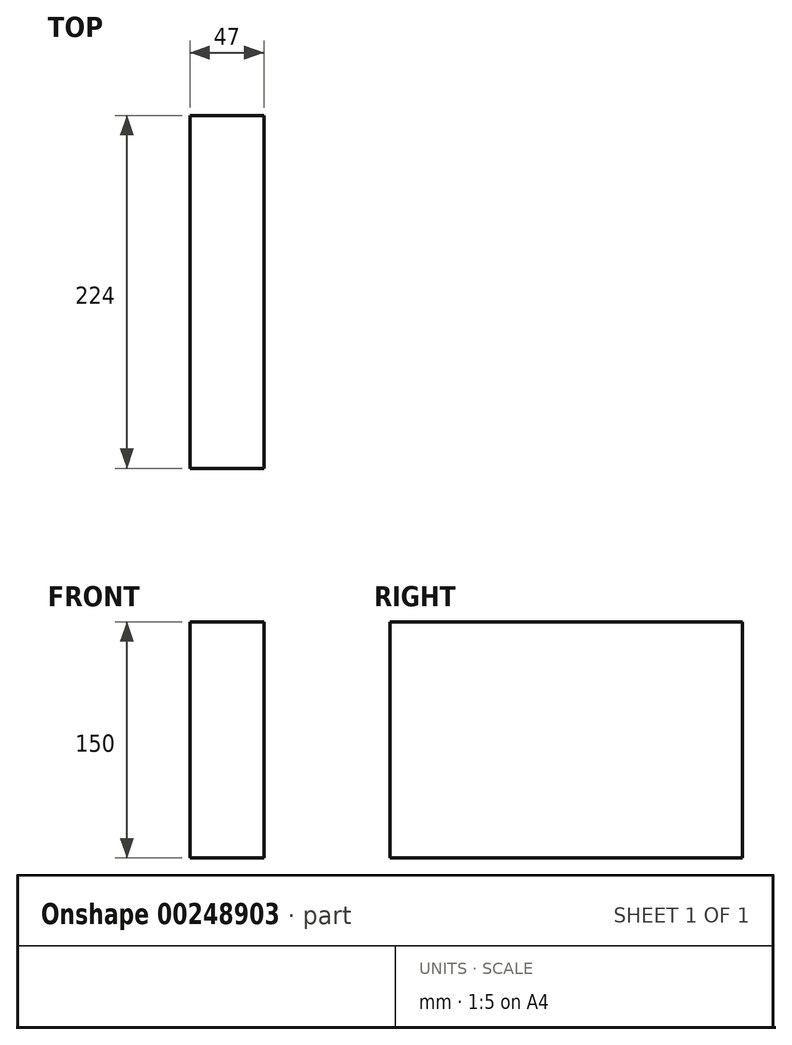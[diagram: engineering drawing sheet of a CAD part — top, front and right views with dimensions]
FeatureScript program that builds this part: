
annotation { "Feature Type Name" : "Feature", "Feature Type Description" : "" }
export const myFeature = defineFeature(function(context is Context, id is Id, definition is map)
    precondition{}
    {
        {
            var Q0;
            Q0=qCreatedBy(makeId("Front.planeOp"),FACE);
            var sketch = newSketch(context, id + "F0", { "sketchPlane" : qUnion([Q0])});
            skLineSegment(sketch, "E0.bottom", {"start": v(0, 0) * mm, "end": v(47, 0) * mm});
            skLineSegment(sketch, "E0.top", {"start": v(0, 150) * mm, "end": v(47, 150) * mm});
            skLineSegment(sketch, "E0.left", {"start": v(0, 0) * mm, "end": v(0, 150) * mm});
            skLineSegment(sketch, "E0.right", {"start": v(47, 0) * mm, "end": v(47, 150) * mm});
            skSolve(sketch);
        }
        {
            var Q0;
            Q0=makeQuery(id+"F0.imprint","IMPRINT",FACE,{"disambiguationData":[TD([[makeQuery(id+"F0.imprint","IMPRINT",EDGE,{"derivedFrom":sQuery(id+"F0.wireOp",EDGE,"E0.bottom")}),1.0]])]});
            extrude(context, id + "F1", {"entities" : qUnion([Q0]), "oppositeDirection" : true, "depth" : 224 * mm});
        }
    });
